# Revit family: ME_Оборудование [водосчетчик универсальный с импульсным выходом без сгонов, VTF-15U-IL] - VALTEC
name_source: partatom
category: Оборудование
revit_build: Autodesk Revit 2018 (Build: 20181011_1500(x64)
units: mm (PartAtom-declared; Revit-internal decimal feet)

## family parameters
Всегда вертикально = Да
Классификация = Нет
На основе рабочей плоскости = Нет
Общий = Нет
При загрузке вырезать с полостями = Нет
Размер круглого соединителя = Использовать диаметр
Тип детали = Вставляется
Точка расчета площади = Нет

## types (1)
- VTF-15U-IL
    ADSK_URL документации изделия = https://valtec.ru
    ADSK_URL страницы изделия = https://valtec.ru
    ADSK_Материал = Сталь, нержавеющая - VALTEC
    ADSK_Потеря давления жидкости = 250.0 Па
    ADSK_Расход жидкости = 0.0 л/с
    D = 15 мм
    L = 80 мм
    URL = https://valtec.ru
    d1 = 15 мм
    d2 = 10 мм
    d3 = 10 мм
    Изготовитель = VALTEC
    Материал доб.1 = Пластик серый - VALTEC
    Материал доб.2 = Пластик белый - VALTEC
    Материал доб.3 = Пластик прозрачный - VALTEC
    Материал доб.4 = Красной - VALTEC
    Показать направление потока = Нет
